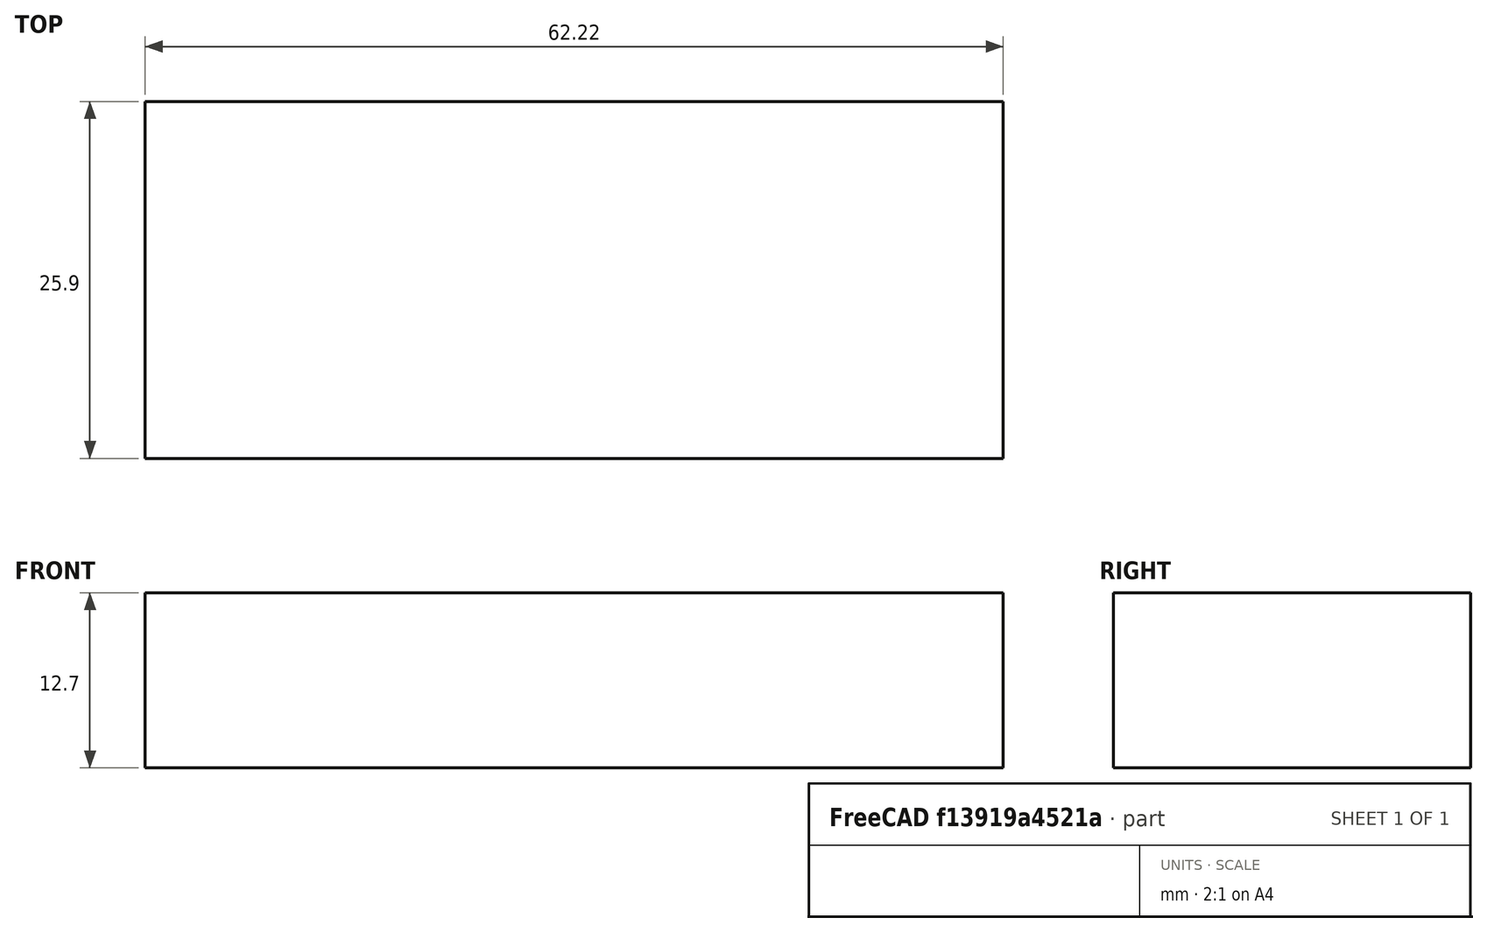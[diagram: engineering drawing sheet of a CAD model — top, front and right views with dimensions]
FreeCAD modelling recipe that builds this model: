
FCSTD DOCUMENT  (FreeCAD 0.15R4671 (Git))
Label: brushless_esc
License: All rights reserved
LicenseURL: http://en.wikipedia.org/wiki/All_rights_reserved
objects: Sketcher::SketchObject×1, PartDesign::Pad×1
note: 3 computed .brp shape members not serialized (recipe doc carries the construction recipe); baked Part::Feature solids carry a one-line shape summary decoded from their .brp

FEATURE [Sketcher::SketchObject] Sketch
  sketch-geometry (4):
    g0: LineSegment StartX=-31.115 StartY=12.954 StartZ=0 EndX=31.115 EndY=12.954 EndZ=0
    g1: LineSegment StartX=31.115 StartY=12.954 StartZ=0 EndX=31.115 EndY=-12.954 EndZ=0
    g2: LineSegment StartX=31.115 StartY=-12.954 StartZ=0 EndX=-31.115 EndY=-12.954 EndZ=0
    g3: LineSegment StartX=-31.115 StartY=-12.954 StartZ=0 EndX=-31.115 EndY=12.954 EndZ=0
  constraints (11):
    c: Coincident(g0,g1)
    c: Coincident(g1,g2)
    c: Coincident(g2,g3)
    c: Coincident(g3,g0)
    c: Horizontal(g0)
    c: Horizontal(g2)
    c: Vertical(g1)
    c: Vertical(g3)
    c: DistanceX(g0) = 62.23
    c: DistanceY(g1) = -25.908
    c: Symmetric(g0,g2,g-1)
FEATURE [PartDesign::Pad] Pad
  Length = 12.7
  Length2 = 100
  Sketch = -> Sketch
  Type = 0
